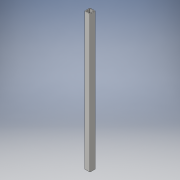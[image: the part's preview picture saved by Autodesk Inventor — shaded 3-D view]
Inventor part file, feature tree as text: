
AUTODESK INVENTOR PART (.ipt)
format: ipt  version: 2016 (Build 200138000, 138)  size: 96,256 bytes
history: native  units: in
note: dims shown in document units (in); Inventor stores cm internally (conversion verified against a paired STEP export)
features: extrude x1, sketch x1
ambient origin geometry x8: Origin, YZ Plane, XZ Plane, XY Plane, X Axis, Y Axis, Z Axis, Center Point
bodies: Solid1 (feature_tree)
feature tree (2):
  extrude  "Extrusion1"  Depth=1.0in
  sketch  "Sketch1"  dims[d0=1.0in d1=1.0in d2=0.125in d4=0.125in d5=0.125in d6=0.125in d7=26.0in d8=0.0in]
